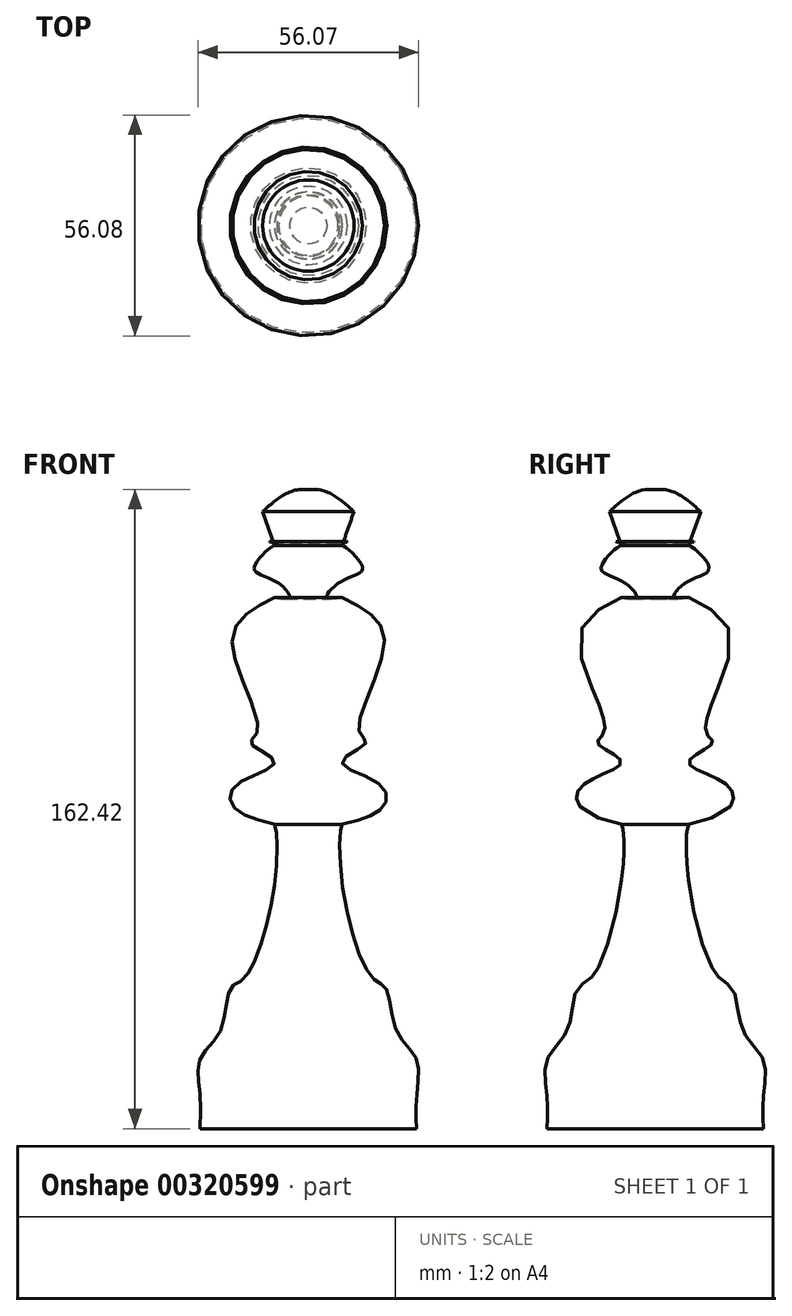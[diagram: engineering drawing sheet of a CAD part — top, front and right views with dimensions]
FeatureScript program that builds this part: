
annotation { "Feature Type Name" : "Feature", "Feature Type Description" : "" }
export const myFeature = defineFeature(function(context is Context, id is Id, definition is map)
    precondition{}
    {
        {
            var Q0;
            Q0=qCreatedBy(makeId("Front.planeOp"),FACE);
            var sketch = newSketch(context, id + "F0", { "sketchPlane" : qUnion([Q0])});
            skLineSegment(sketch, "E0", {"start": v(-45.65, -71.53) * mm, "end": v(-73.14, -71.53) * mm});
            skFitSpline(sketch, "E1", {"points": [v(-73.14, -71.53) * mm, v(-73.14, -63.37) * mm, v(-73.14, -53.91) * mm, v(-67.99, -46.61) * mm, v(-65.4, -35.87) * mm, v(-61.97, -33.3) * mm, v(-54.24, -9.24) * mm, v(-54.24, 5.8) * mm, v(-54.67, 5.8) * mm], "startDerivative": vector(3.41, 65.13) * mm, "endDerivative": vector(-16.26, -6.36) * mm});
            skFitSpline(sketch, "E2", {"points": [v(-54.24, 5.8) * mm, v(-64.55, 10.1) * mm, v(-64.12, 15.68) * mm, v(-54.24, 21.7) * mm, v(-60.25, 26.42) * mm, v(-58.53, 29.43) * mm, v(-64.98, 52.63) * mm, v(-54.24, 63.37) * mm], "startDerivative": vector(-85.05, 20.55) * mm, "endDerivative": vector(91.46, 44.6) * mm});
            skFitSpline(sketch, "E3", {"points": [v(-54.24, 63.37) * mm, v(-50.37, 63.37) * mm, v(-54.24, 67.66) * mm, v(-59.4, 71.1) * mm, v(-54.24, 76.68) * mm, v(-54.24, 76.25) * mm], "startDerivative": vector(27.98, -5.02) * mm, "endDerivative": vector(-3.27, -10) * mm});
            skFitSpline(sketch, "E4", {"points": [v(-54.24, 76.68) * mm, v(-57.25, 85.27) * mm], "startDerivative": vector(-3, 8.6) * mm, "endDerivative": vector(-3, 8.6) * mm});
            skFitSpline(sketch, "E5", {"points": [v(-57.25, 85.27) * mm, v(-47.8, 90.86) * mm, v(-32.76, 85.27) * mm], "startDerivative": vector(19.38, 17.44) * mm, "endDerivative": vector(29.28, -16.37) * mm});
            skFitSpline(sketch, "E6", {"points": [v(-32.76, 85.27) * mm, v(-32.76, 79.26) * mm, v(-38.1, 77.11) * mm], "startDerivative": vector(2.73, -13.8) * mm, "endDerivative": vector(-13.47, -2.48) * mm});
            skFitSpline(sketch, "E7", {"points": [v(-38.1, 77.11) * mm, v(-32.76, 77.11) * mm, v(-28.9, 70.67) * mm, v(-32.76, 66.37) * mm, v(-38.1, 65.08) * mm], "startDerivative": vector(22.88, 5.88) * mm, "endDerivative": vector(-22.26, -2.97) * mm});
            skLineSegment(sketch, "E8", {"start": v(-45.65, 123.08) * mm, "end": v(-45.65, -96.01) * mm, "construction": true});
            skPoint(sketch, "E9.1.internal.orphan", {"position": v(-25.46, 56.92) * mm});
            skPoint(sketch, "E9.endDerivative.orphan", {"position": v(-32.92, 23.95) * mm});
            skPoint(sketch, "E10.1.internal.orphan", {"position": v(-25.46, 13.53) * mm});
            skPoint(sketch, "E10.2.internal.orphan", {"position": v(-32.92, 6.23) * mm});
            skPoint(sketch, "E10.3.internal.orphan", {"position": v(-25.46, -35.87) * mm});
            skLineSegment(sketch, "E11", {"start": v(-45.65, 90.8) * mm, "end": v(-45.65, -71.53) * mm});
            skSolve(sketch);
        }
        {
            var Q0;
            Q0 = qSketchRegion(id + "F0", true);
            var Q1;
            Q1=sQuery(id+"F0.wireOp",EDGE,"E8");
            revolve(context, id + "F1", {"entities" : qUnion([Q0]), "axis" : qUnion([Q1]), "revolveType" : RevolveType.FULL});
        }
    });
